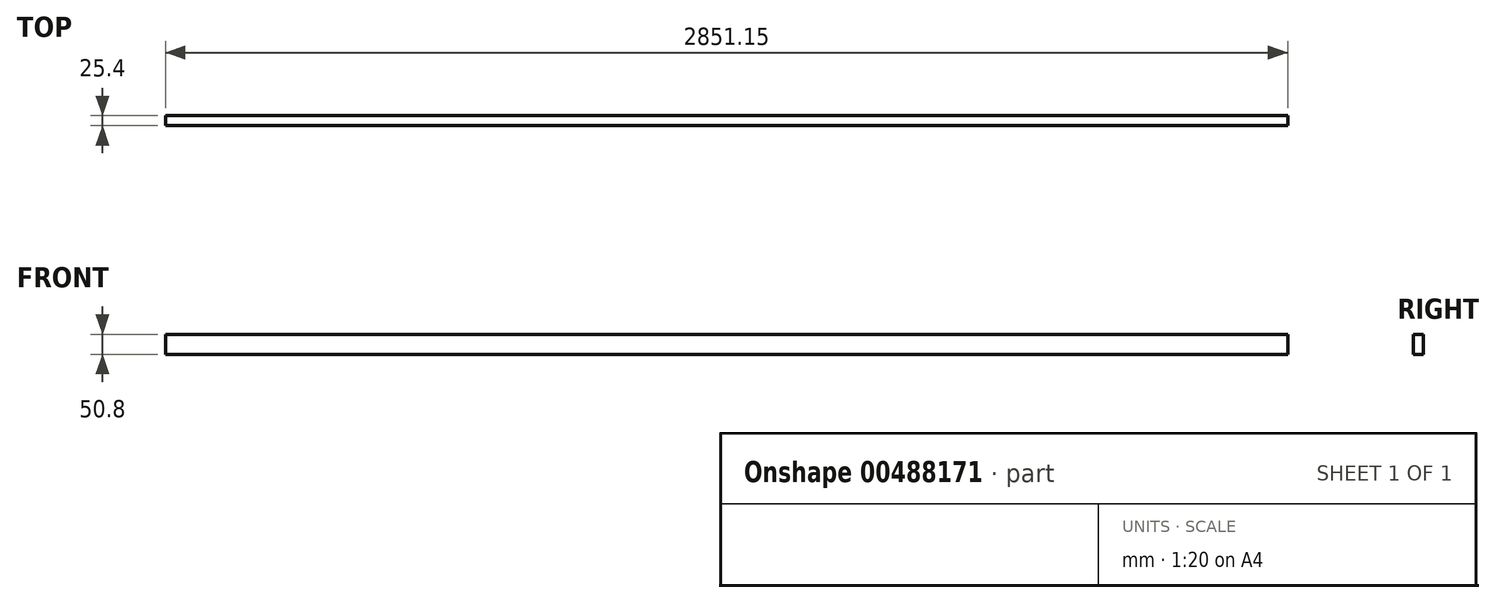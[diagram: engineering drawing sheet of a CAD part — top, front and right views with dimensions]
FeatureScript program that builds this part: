
annotation { "Feature Type Name" : "Feature", "Feature Type Description" : "" }
export const myFeature = defineFeature(function(context is Context, id is Id, definition is map)
    precondition{}
    {
        {
            var Q0;
            Q0=qCreatedBy(makeId("Front.planeOp"),FACE);
            var sketch = newSketch(context, id + "F0", { "sketchPlane" : qUnion([Q0])});
            skLineSegment(sketch, "E0", {"start": v(0, 0) * mm, "end": v(0, 50.8) * mm});
            skLineSegment(sketch, "E1", {"start": v(0, 50.8) * mm, "end": v(25.4, 50.8) * mm});
            skLineSegment(sketch, "E2", {"start": v(25.4, 50.8) * mm, "end": v(25.4, 0) * mm});
            skLineSegment(sketch, "E3", {"start": v(25.4, 0) * mm, "end": v(0, 0) * mm});
            skSolve(sketch);
        }
        {
            var Q0;
            Q0=makeQuery(id+"F0.imprint","IMPRINT",FACE,{"disambiguationData":[TD([[makeQuery(id+"F0.imprint","IMPRINT",EDGE,{"derivedFrom":sQuery(id+"F0.wireOp",EDGE,"E0")}),-1.0]])]});
            extrude(context, id + "F1", {"entities" : qUnion([Q0]), "depth" : 25.4 * mm, "offsetDistance" : 25.4 * mm});
        }
        {
            var Q0;
            Q0=makeQuery(id+"F1.opExtrude","SWEPT_FACE",FACE,{"disambiguationData":[OSD([sQuery(id+"F0.wireOp",EDGE,"E2")])]});
            extrude(context, id + "F2", {"entities" : qUnion([Q0]), "operationType" : NewBodyOperationType.ADD, "depth" : 2870.2 * mm - 44.45 * mm, "offsetDistance" : 25.4 * mm});
        }
    });
